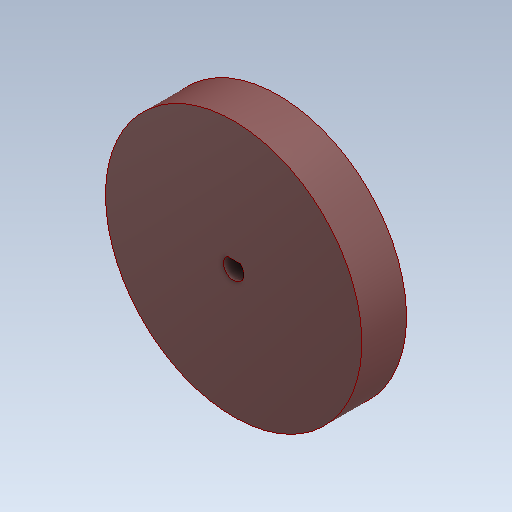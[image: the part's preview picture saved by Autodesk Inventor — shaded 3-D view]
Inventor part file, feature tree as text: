
AUTODESK INVENTOR PART (.ipt)
format: ipt  version: 2020 (Build 240168000, 168)  size: 107,008 bytes
history: native  units: mm
features: other x1, extrude x1, sketch x1, imported_body x1
ambient origin geometry x8: Origin, YZ Plane, XZ Plane, XY Plane, X Axis, Y Axis, Z Axis, Center Point
bodies: Body1 (feature_tree)
feature tree (4):
  other  "Твердое тело1"
  extrude  "Выдавливание1"  Depth=50.0mm
  sketch  "Эскиз1"
  imported_body  "БазТело1"
